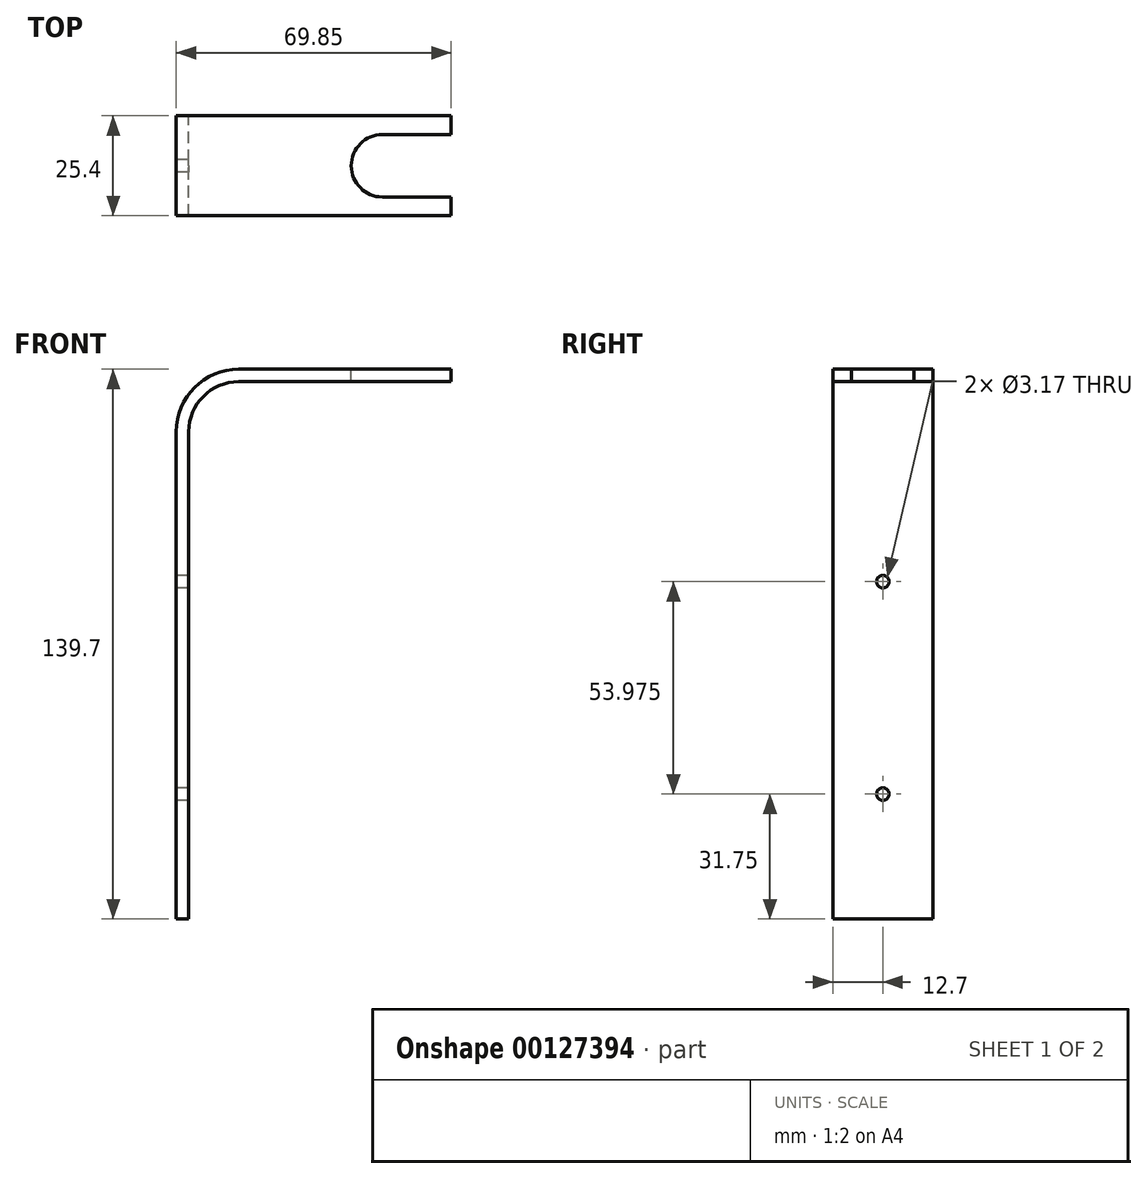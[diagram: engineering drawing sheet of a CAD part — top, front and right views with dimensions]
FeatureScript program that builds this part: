
annotation { "Feature Type Name" : "Feature", "Feature Type Description" : "" }
export const myFeature = defineFeature(function(context is Context, id is Id, definition is map)
    precondition{}
    {
        {
            var Q0;
            Q0=qCreatedBy(makeId("Front.planeOp"),FACE);
            var sketch = newSketch(context, id + "F0", { "sketchPlane" : qUnion([Q0])});
            skLineSegment(sketch, "E0.bottom", {"start": v(15.88, 0) * mm, "end": v(69.85, 0) * mm});
            skLineSegment(sketch, "E0.top", {"start": v(0, -139.7) * mm, "end": v(69.85, -139.7) * mm, "construction": true});
            skLineSegment(sketch, "E0.left", {"start": v(0, -15.88) * mm, "end": v(0, -139.7) * mm});
            skLineSegment(sketch, "E0.right", {"start": v(69.85, 0) * mm, "end": v(69.85, -139.7) * mm, "construction": true});
            skPoint(sketch, "E1.visualSharp", {"position": v(0, 0) * mm});
            skArc(sketch, "E1.filletArc", {"start": v(15.88, 0) * mm, "mid": v(4.65, -4.65) * mm, "end": v(0, -15.87) * mm});
            skLineSegment(sketch, "E2.0", {"start": v(15.88, -3.18) * mm, "end": v(69.85, -3.18) * mm});
            skArc(sketch, "E2.1", {"start": v(15.88, -3.17) * mm, "mid": v(6.9, -6.9) * mm, "end": v(3.18, -15.88) * mm});
            skLineSegment(sketch, "E2.2", {"start": v(3.18, -15.88) * mm, "end": v(3.18, -139.7) * mm});
            skLineSegment(sketch, "E3", {"start": v(69.85, 0) * mm, "end": v(69.85, -3.18) * mm});
            skLineSegment(sketch, "E4", {"start": v(3.18, -139.7) * mm, "end": v(0, -139.7) * mm});
            skSolve(sketch);
        }
        {
            var Q0;
            Q0=makeQuery(id+"F0.imprint","IMPRINT",FACE,{"disambiguationData":[TD([[makeQuery(id+"F0.imprint","IMPRINT",EDGE,{"derivedFrom":sQuery(id+"F0.wireOp",EDGE,"E0.bottom")}),-1.0]])]});
            extrude(context, id + "F1", {"entities" : qUnion([Q0]), "endBound" : BoundingType.SYMMETRIC, "depth" : 25.4 * mm});
        }
        {
            var Q0;
            Q0=makeQuery(id+"F1.opExtrude","SWEPT_FACE",FACE,{"disambiguationData":[OSD([sQuery(id+"F0.wireOp",EDGE,"E0.bottom")])]});
            var sketch = newSketch(context, id + "F2", { "sketchPlane" : qUnion([Q0])});
            skCircle(sketch, "E5", {"center": v(52.39, 0) * mm, "radius": 7.94 * mm});
            skLineSegment(sketch, "E6", {"start": v(52.39, 7.94) * mm, "end": v(69.85, 7.94) * mm});
            skLineSegment(sketch, "E7", {"start": v(69.85, 7.94) * mm, "end": v(69.85, -7.94) * mm});
            skLineSegment(sketch, "E8", {"start": v(69.85, -7.94) * mm, "end": v(52.39, -7.94) * mm});
            skLineSegment(sketch, "E9", {"start": v(52.39, -7.94) * mm, "end": v(52.39, 7.94) * mm, "construction": true});
            skSolve(sketch);
        }
        {
            var Q0;
            {var subQ0=sQuery(id+"F2.wireOp",EDGE,"E5");var subQ1=makeQuery(id+"F2.imprint","INTERSECT",VERTEX,{"derivedFrom":[subQ0,sQuery(id+"F2.wireOp",EDGE,"E6")]});Q0=makeQuery(id+"F2.imprint","IMPRINT",FACE,{"disambiguationData":[TD([[makeQuery(id+"F2.imprint","IMPRINT",EDGE,{"disambiguationData":[TD([[subQ1,-1.0]])],"derivedFrom":subQ0}),1.0]])]});}
            var Q1;
            {var subQ0=sQuery(id+"F2.wireOp",EDGE,"E6");Q1=makeQuery(id+"F2.imprint","IMPRINT",FACE,{"disambiguationData":[TD([[makeQuery(id+"F2.imprint","IMPRINT",EDGE,{"derivedFrom":subQ0}),-1.0]])]});}
            extrude(context, id + "F3", {"entities" : qUnion([Q0, Q1]), "operationType" : NewBodyOperationType.REMOVE, "oppositeDirection" : true, "depth" : 25.4 * mm});
        }
        {
            var Q0;
            Q0=makeQuery(id+"F1.opExtrude","SWEPT_FACE",FACE,{"disambiguationData":[OSD([sQuery(id+"F0.wireOp",EDGE,"E0.left")])]});
            var sketch = newSketch(context, id + "F4", { "sketchPlane" : qUnion([Q0])});
            skLineSegment(sketch, "E10", {"start": v(0, -139.7) * mm, "end": v(0, -107.95) * mm, "construction": true});
            skPoint(sketch, "E10.endSnap0", {"position": v(0, -139.7) * mm});
            skLineSegment(sketch, "E11", {"start": v(0, -107.95) * mm, "end": v(0, -53.98) * mm, "construction": true});
            skCircle(sketch, "E12", {"center": v(0, -53.98) * mm, "radius": 1.59 * mm});
            skCircle(sketch, "E13", {"center": v(0, -107.95) * mm, "radius": 1.59 * mm});
            skSolve(sketch);
        }
        {
            var Q0;
            Q0 = qSketchRegion(id + "F4", true);
            extrude(context, id + "F5", {"entities" : qUnion([Q0]), "operationType" : NewBodyOperationType.REMOVE, "oppositeDirection" : true, "depth" : 25.4 * mm});
        }
    });
